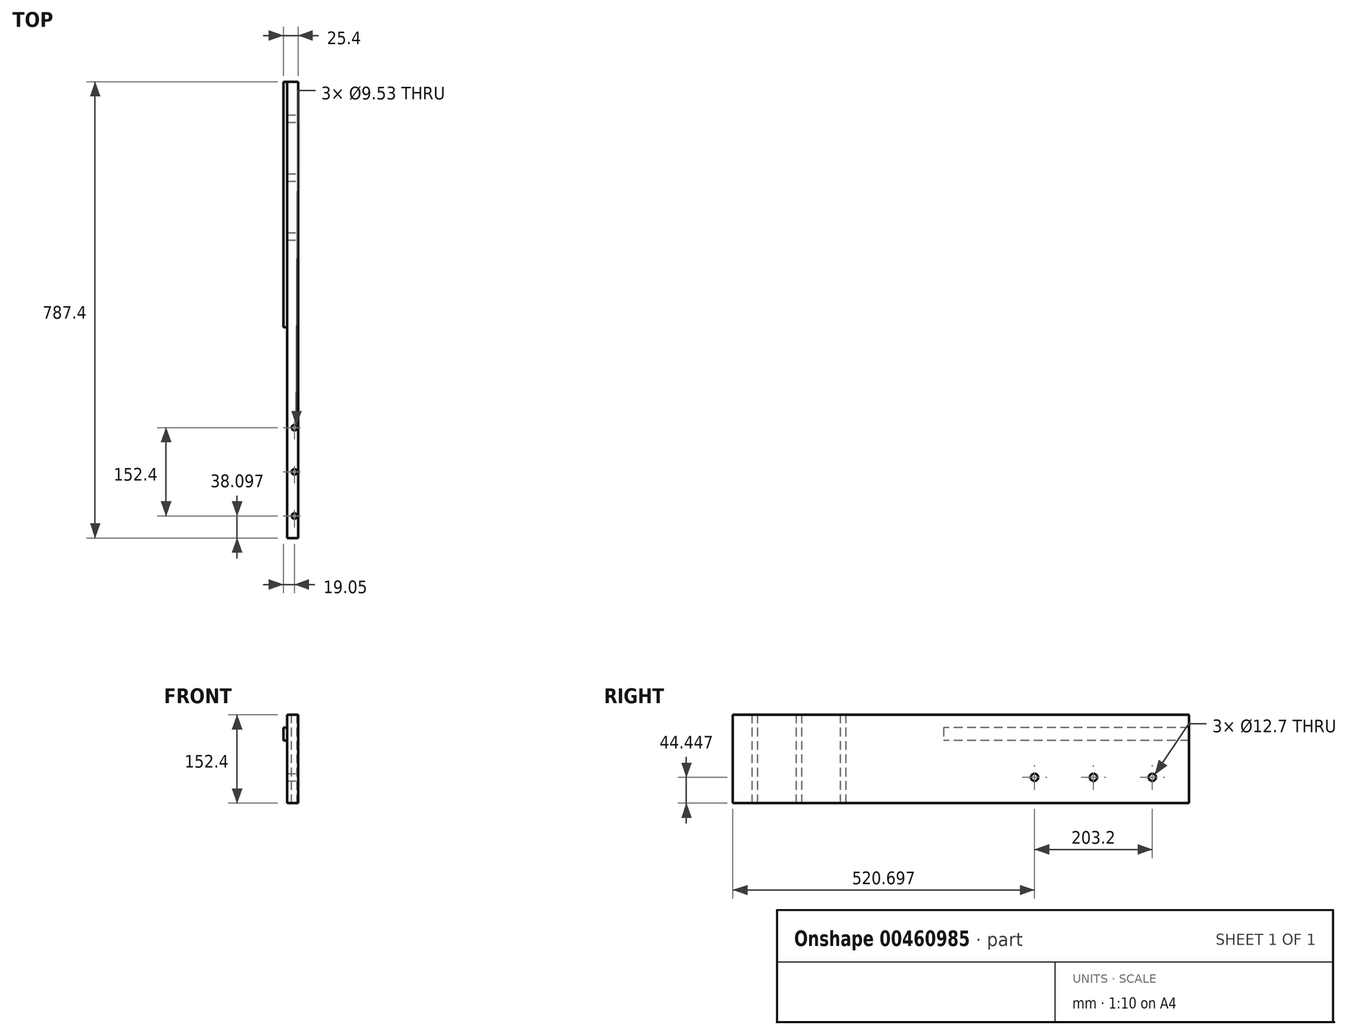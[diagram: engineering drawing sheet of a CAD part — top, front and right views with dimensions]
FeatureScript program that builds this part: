
annotation { "Feature Type Name" : "Feature", "Feature Type Description" : "" }
export const myFeature = defineFeature(function(context is Context, id is Id, definition is map)
    precondition{}
    {
        {
            var Q0;
            Q0=qCreatedBy(makeId("Right.planeOp"),FACE);
            var sketch = newSketch(context, id + "F0", { "sketchPlane" : qUnion([Q0])});
            skLineSegment(sketch, "E0.bottom", {"start": v(-363.93, 130.34) * mm, "end": v(423.47, 130.34) * mm});
            skLineSegment(sketch, "E0.top", {"start": v(-363.93, -22.06) * mm, "end": v(423.47, -22.06) * mm});
            skLineSegment(sketch, "E0.left", {"start": v(-363.93, 130.34) * mm, "end": v(-363.93, -22.06) * mm});
            skLineSegment(sketch, "E0.right", {"start": v(423.47, 130.34) * mm, "end": v(423.47, -22.06) * mm});
            skSolve(sketch);
        }
        {
            var Q0;
            Q0=makeQuery(id+"F0.imprint","IMPRINT",FACE,{"disambiguationData":[TD([[makeQuery(id+"F0.imprint","IMPRINT",EDGE,{"derivedFrom":sQuery(id+"F0.wireOp",EDGE,"E0.bottom")}),-1.0]])]});
            extrude(context, id + "F1", {"entities" : qUnion([Q0]), "depth" : 19.05 * mm});
        }
        {
            var Q0;
            Q0=makeQuery(id+"F1.opExtrude","CAP_FACE",FACE,{"disambiguationData":[OSD([sQuery(id+"F0.wireOp",EDGE,"E0.bottom"),sQuery(id+"F0.wireOp",EDGE,"E0.top"),sQuery(id+"F0.wireOp",EDGE,"E0.left"),sQuery(id+"F0.wireOp",EDGE,"E0.right")])],"isStart":false});
            var sketch = newSketch(context, id + "F2", { "sketchPlane" : qUnion([Q0])});
            skPoint(sketch, "E1", {"position": v(359.97, 22.39) * mm});
            skPoint(sketch, "E2", {"position": v(258.37, 22.39) * mm});
            skPoint(sketch, "E3", {"position": v(156.77, 22.39) * mm});
            skSolve(sketch);
        }
        {
            var Q0;
            Q0=makeQuery(id+"F1.opExtrude","SWEPT_FACE",FACE,{"disambiguationData":[OSD([sQuery(id+"F0.wireOp",EDGE,"E0.bottom")])]});
            var sketch = newSketch(context, id + "F3", { "sketchPlane" : qUnion([Q0])});
            skPoint(sketch, "E4", {"position": v(12.7, -325.83) * mm});
            skPoint(sketch, "E5", {"position": v(12.7, -249.63) * mm});
            skPoint(sketch, "E6", {"position": v(12.7, -173.43) * mm});
            skSolve(sketch);
        }
        {
            var Q0;
            Q0=sQuery(id+"F2.wireOp",VERTEX,"E3");
            var Q1;
            Q1=sQuery(id+"F2.wireOp",VERTEX,"E2");
            var Q2;
            Q2=sQuery(id+"F2.wireOp",VERTEX,"E1");
            var Q3;
            Q3=makeQuery(id+"F1.opExtrude","SWEPT_BODY",BODY,{"disambiguationData":[OSD([sQuery(id+"F0.wireOp",EDGE,"E0.bottom"),sQuery(id+"F0.wireOp",EDGE,"E0.top"),sQuery(id+"F0.wireOp",EDGE,"E0.left"),sQuery(id+"F0.wireOp",EDGE,"E0.right")])]});
            hole(context, id + "F4", {"style" : HoleStyle.SIMPLE, "endStyle" : HoleEndStyle.THROUGH, "holeDiameter" : 12.7 * mm, "isTappedThrough" : true, "tappedDepth" : 12.7 * mm, "tapClearance" : 3, "startFromSketch" : true, "locations" : qUnion([Q0, Q1, Q2]), "scope" : qUnion([Q3])});
        }
        {
            var Q0;
            Q0=sQuery(id+"F3.wireOp",VERTEX,"E6");
            var Q1;
            Q1=sQuery(id+"F3.wireOp",VERTEX,"E5");
            var Q2;
            Q2=sQuery(id+"F3.wireOp",VERTEX,"E4");
            var Q3;
            Q3=makeQuery(id+"F1.opExtrude","SWEPT_BODY",BODY,{"disambiguationData":[OSD([sQuery(id+"F0.wireOp",EDGE,"E0.bottom"),sQuery(id+"F0.wireOp",EDGE,"E0.top"),sQuery(id+"F0.wireOp",EDGE,"E0.left"),sQuery(id+"F0.wireOp",EDGE,"E0.right")])]});
            hole(context, id + "F5", {"style" : HoleStyle.SIMPLE, "endStyle" : HoleEndStyle.THROUGH, "holeDiameter" : 9.52 * mm, "isTappedThrough" : true, "tappedDepth" : 12.7 * mm, "tapClearance" : 3, "startFromSketch" : true, "locations" : qUnion([Q0, Q1, Q2]), "scope" : qUnion([Q3])});
        }
        {
            var Q0;
            Q0=makeQuery(id+"F1.opExtrude","CAP_FACE",FACE,{"disambiguationData":[OSD([sQuery(id+"F0.wireOp",EDGE,"E0.bottom"),sQuery(id+"F0.wireOp",EDGE,"E0.top"),sQuery(id+"F0.wireOp",EDGE,"E0.left"),sQuery(id+"F0.wireOp",EDGE,"E0.right")])],"isStart":true});
            var sketch = newSketch(context, id + "F6", { "sketchPlane" : qUnion([Q0])});
            skLineSegment(sketch, "E7", {"start": v(-359.97, 22.39) * mm, "end": v(-163.12, 22.39) * mm});
            skLineSegment(sketch, "E8.0", {"start": v(-423.47, 108.11) * mm, "end": v(0, 108.11) * mm});
            skLineSegment(sketch, "E9", {"start": v(0, 108.11) * mm, "end": v(0, 85.89) * mm});
            skLineSegment(sketch, "E10", {"start": v(-423.47, 85.89) * mm, "end": v(-423.47, 108.11) * mm});
            skLineSegment(sketch, "E11.0", {"start": v(-423.47, 85.89) * mm, "end": v(0, 85.89) * mm});
            skPoint(sketch, "E12.orphan", {"position": v(0, 82.71) * mm});
            skSolve(sketch);
        }
        {
            var Q0;
            Q0=makeQuery(id+"F6.imprint","IMPRINT",FACE,{"disambiguationData":[TD([[makeQuery(id+"F6.imprint","IMPRINT",EDGE,{"derivedFrom":sQuery(id+"F6.wireOp",EDGE,"E8.0")}),-1.0]])]});
            extrude(context, id + "F7", {"entities" : qUnion([Q0]), "operationType" : NewBodyOperationType.ADD, "depth" : 12.7 * mm, "offsetDistance" : 25.4 * mm, "symmetric" : true});
        }
    });
